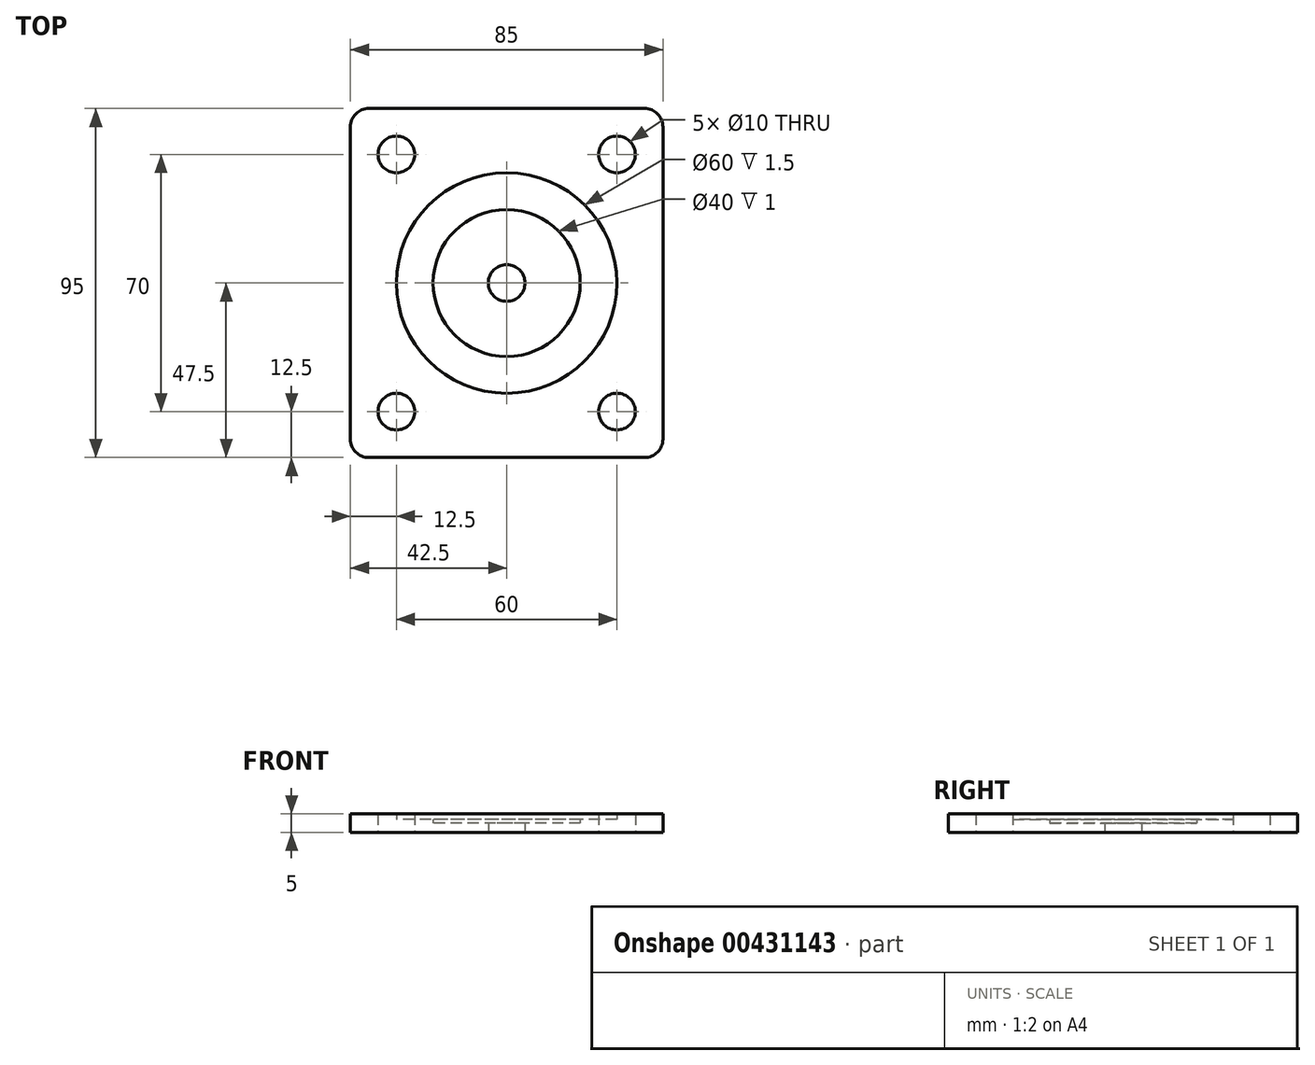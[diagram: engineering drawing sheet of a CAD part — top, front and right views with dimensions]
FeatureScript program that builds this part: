
annotation { "Feature Type Name" : "Feature", "Feature Type Description" : "" }
export const myFeature = defineFeature(function(context is Context, id is Id, definition is map)
    precondition{}
    {
        {
            var Q0;
            Q0=qCreatedBy(makeId("Top.planeOp"),FACE);
            var sketch = newSketch(context, id + "F0", { "sketchPlane" : qUnion([Q0])});
            skLineSegment(sketch, "E0.bottom", {"start": v(42.5, 47.5) * mm, "end": v(-42.5, 47.5) * mm});
            skLineSegment(sketch, "E0.top", {"start": v(42.5, -47.5) * mm, "end": v(-42.5, -47.5) * mm});
            skLineSegment(sketch, "E0.left", {"start": v(42.5, 47.5) * mm, "end": v(42.5, -47.5) * mm});
            skLineSegment(sketch, "E0.right", {"start": v(-42.5, 47.5) * mm, "end": v(-42.5, -47.5) * mm});
            skPoint(sketch, "E0.middle", {"position": v(0, 0) * mm});
            skLineSegment(sketch, "E1", {"start": v(0, 0) * mm, "end": v(0, 47.5) * mm, "construction": true});
            skLineSegment(sketch, "E2", {"start": v(0, 0) * mm, "end": v(-42.5, 0) * mm, "construction": true});
            skLineSegment(sketch, "E3", {"start": v(42.5, 0) * mm, "end": v(0, 0) * mm, "construction": true});
            skLineSegment(sketch, "E4", {"start": v(0, 0) * mm, "end": v(0, -47.5) * mm, "construction": true});
            skCircle(sketch, "E5", {"center": v(-30, 35) * mm, "radius": 5 * mm});
            skCircle(sketch, "E6.MirrorC", {"center": v(30, 35) * mm, "radius": 5 * mm});
            skLineSegment(sketch, "E7.MirrorCS", {"start": v(-42.5, 0) * mm, "end": v(0, 0) * mm, "construction": true});
            skCircle(sketch, "E8.MirrorC", {"center": v(30, -35) * mm, "radius": 5 * mm});
            skCircle(sketch, "E9.MirrorC", {"center": v(-30, -35) * mm, "radius": 5 * mm});
            skCircle(sketch, "E10", {"center": v(0, 0) * mm, "radius": 30 * mm});
            skCircle(sketch, "E11", {"center": v(0, 0) * mm, "radius": 5 * mm});
            skCircle(sketch, "E12", {"center": v(0, 0) * mm, "radius": 20 * mm});
            skSolve(sketch);
        }
        {
            var Q0;
            Q0=makeQuery(id+"F0.imprint","IMPRINT",FACE,{"disambiguationData":[TD([[makeQuery(id+"F0.imprint","IMPRINT",EDGE,{"derivedFrom":sQuery(id+"F0.wireOp",EDGE,"E0.bottom")}),1.0]])]});
            extrude(context, id + "F1", {"entities" : qUnion([Q0]), "depth" : 5 * mm});
        }
        {
            var Q0;
            Q0=makeQuery(id+"F0.imprint","IMPRINT",FACE,{"disambiguationData":[TD([[makeQuery(id+"F0.imprint","IMPRINT",EDGE,{"derivedFrom":sQuery(id+"F0.wireOp",EDGE,"E10")}),1.0]])]});
            var Q1;
            Q1=makeQuery(id+"F0.imprint","IMPRINT",FACE,{"disambiguationData":[TD([[makeQuery(id+"F0.imprint","IMPRINT",EDGE,{"derivedFrom":sQuery(id+"F0.wireOp",EDGE,"E11")}),-1.0]])]});
            extrude(context, id + "F2", {"entities" : qUnion([Q0, Q1]), "operationType" : NewBodyOperationType.ADD, "depth" : 2.5 * mm});
        }
        {
            var Q0;
            Q0=makeQuery(id+"F0.imprint","IMPRINT",FACE,{"disambiguationData":[TD([[makeQuery(id+"F0.imprint","IMPRINT",EDGE,{"derivedFrom":sQuery(id+"F0.wireOp",EDGE,"E10")}),1.0]])]});
            extrude(context, id + "F3", {"entities" : qUnion([Q0]), "operationType" : NewBodyOperationType.ADD, "depth" : 3.5 * mm});
        }
        {
            var Q0;
            Q0=makeQuery(id+"F1.opExtrude","SWEPT_EDGE",EDGE,{"disambiguationData":[OSD([sQuery(id+"F0.wireOp",EDGE,"E0.top"),sQuery(id+"F0.wireOp",EDGE,"E0.right")])]});
            var Q1;
            Q1=makeQuery(id+"F1.opExtrude","SWEPT_EDGE",EDGE,{"disambiguationData":[OSD([sQuery(id+"F0.wireOp",EDGE,"E0.top"),sQuery(id+"F0.wireOp",EDGE,"E0.left")])]});
            var Q2;
            Q2=makeQuery(id+"F1.opExtrude","SWEPT_EDGE",EDGE,{"disambiguationData":[OSD([sQuery(id+"F0.wireOp",EDGE,"E0.bottom"),sQuery(id+"F0.wireOp",EDGE,"E0.left")])]});
            var Q3;
            Q3=makeQuery(id+"F1.opExtrude","SWEPT_EDGE",EDGE,{"disambiguationData":[OSD([sQuery(id+"F0.wireOp",EDGE,"E0.bottom"),sQuery(id+"F0.wireOp",EDGE,"E0.right")])]});
            fillet(context, id + "F4", {"entities" : qUnion([Q0, Q1, Q2, Q3]), "radius" : 5 * mm, "tangentPropagation" : true, "allowEdgeOverflow" : false});
        }
    });
